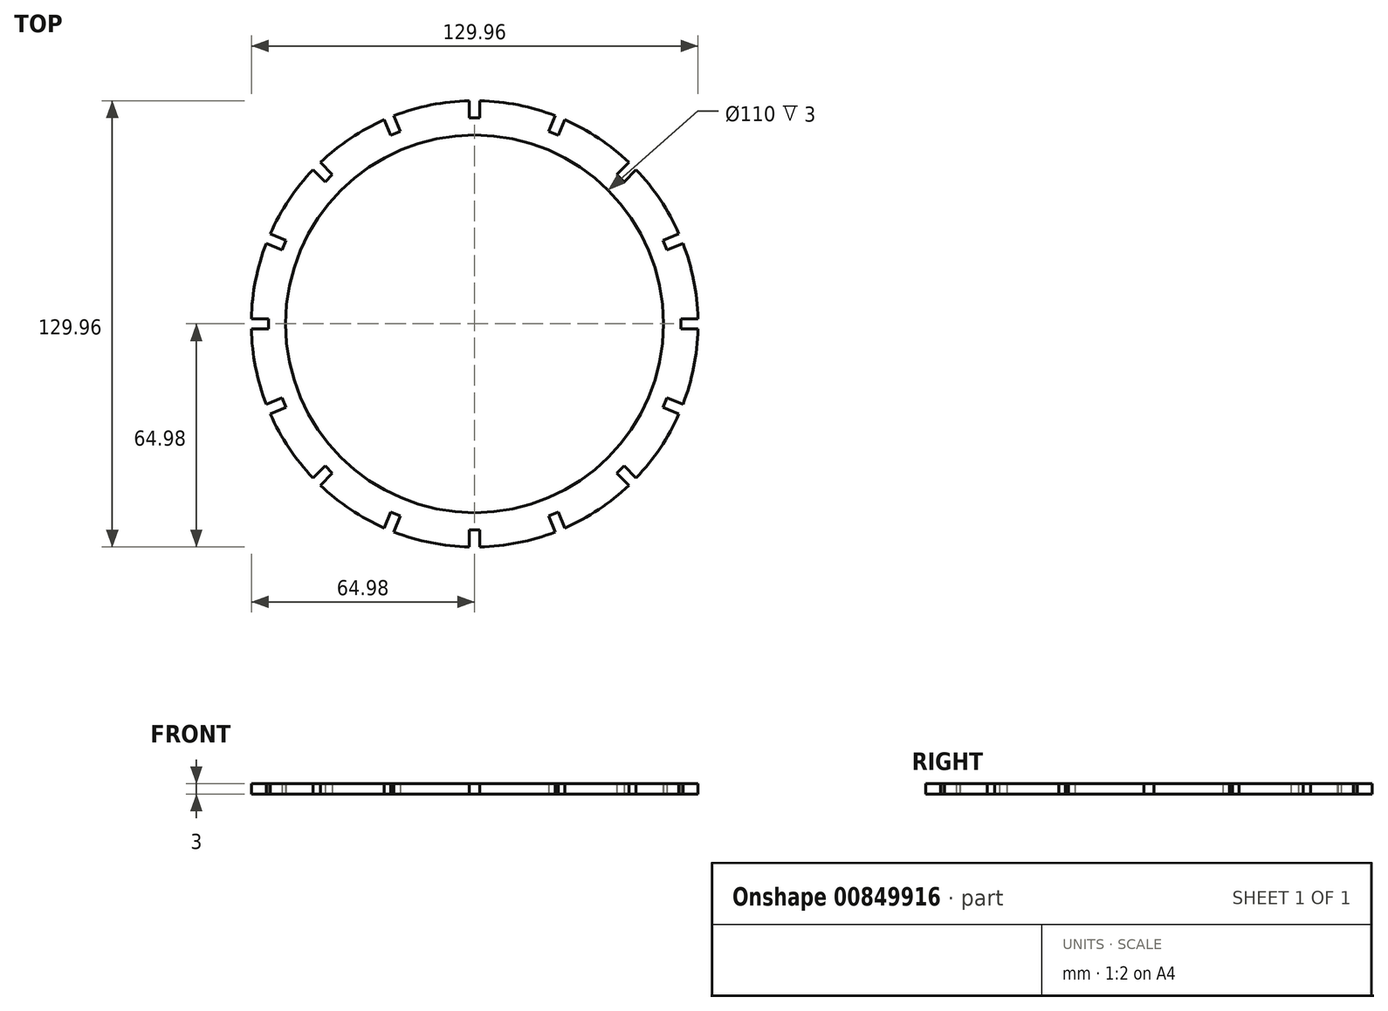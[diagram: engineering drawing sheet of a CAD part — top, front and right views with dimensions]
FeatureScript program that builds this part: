
annotation { "Feature Type Name" : "Feature", "Feature Type Description" : "" }
export const myFeature = defineFeature(function(context is Context, id is Id, definition is map)
    precondition{}
    {
        {
            var Q0;
            Q0=qCreatedBy(makeId("Top.planeOp"),FACE);
            var sketch = newSketch(context, id + "F0", { "sketchPlane" : qUnion([Q0])});
            skCircle(sketch, "E0", {"center": v(0, 0) * mm, "radius": 55 * mm});
            skCircle(sketch, "E1", {"center": v(0, 0) * mm, "radius": 65 * mm});
            skLineSegment(sketch, "E2", {"start": v(0, -60) * mm, "end": v(-1.5, -60) * mm});
            skLineSegment(sketch, "E3", {"start": v(-1.5, -60) * mm, "end": v(1.5, -60) * mm});
            skLineSegment(sketch, "E4", {"start": v(1.5, -60) * mm, "end": v(1.5, -64.98) * mm});
            skLineSegment(sketch, "E5", {"start": v(-1.5, -60) * mm, "end": v(-1.5, -64.98) * mm});
            skLineSegment(sketch, "E6.1.0", {"start": v(21.58, -56) * mm, "end": v(24.35, -54.86) * mm});
            skLineSegment(sketch, "E6.1.1", {"start": v(24.35, -54.86) * mm, "end": v(26.25, -59.46) * mm});
            skLineSegment(sketch, "E6.1.2", {"start": v(21.58, -56) * mm, "end": v(23.48, -60.61) * mm});
            skLineSegment(sketch, "E6.2.0", {"start": v(41.37, -43.49) * mm, "end": v(43.49, -41.37) * mm});
            skLineSegment(sketch, "E6.2.1", {"start": v(43.49, -41.37) * mm, "end": v(47.01, -44.89) * mm});
            skLineSegment(sketch, "E6.2.2", {"start": v(41.37, -43.49) * mm, "end": v(44.89, -47.01) * mm});
            skLineSegment(sketch, "E6.3.0", {"start": v(54.86, -24.35) * mm, "end": v(56, -21.58) * mm});
            skLineSegment(sketch, "E6.3.1", {"start": v(56, -21.58) * mm, "end": v(60.61, -23.48) * mm});
            skLineSegment(sketch, "E6.3.2", {"start": v(54.86, -24.35) * mm, "end": v(59.46, -26.25) * mm});
            skLineSegment(sketch, "E6.4.0", {"start": v(60, -1.5) * mm, "end": v(60, 1.5) * mm});
            skLineSegment(sketch, "E6.4.1", {"start": v(60, 1.5) * mm, "end": v(64.98, 1.5) * mm});
            skLineSegment(sketch, "E6.4.2", {"start": v(60, -1.5) * mm, "end": v(64.98, -1.5) * mm});
            skLineSegment(sketch, "E6.5.0", {"start": v(56, 21.58) * mm, "end": v(54.86, 24.35) * mm});
            skLineSegment(sketch, "E6.5.1", {"start": v(54.86, 24.35) * mm, "end": v(59.46, 26.25) * mm});
            skLineSegment(sketch, "E6.5.2", {"start": v(56, 21.58) * mm, "end": v(60.61, 23.48) * mm});
            skLineSegment(sketch, "E6.6.0", {"start": v(43.49, 41.37) * mm, "end": v(41.37, 43.49) * mm});
            skLineSegment(sketch, "E6.6.1", {"start": v(41.37, 43.49) * mm, "end": v(44.89, 47.01) * mm});
            skLineSegment(sketch, "E6.6.2", {"start": v(43.49, 41.37) * mm, "end": v(47.01, 44.89) * mm});
            skLineSegment(sketch, "E6.7.0", {"start": v(24.35, 54.86) * mm, "end": v(21.58, 56) * mm});
            skLineSegment(sketch, "E6.7.1", {"start": v(21.58, 56) * mm, "end": v(23.48, 60.61) * mm});
            skLineSegment(sketch, "E6.7.2", {"start": v(24.35, 54.86) * mm, "end": v(26.25, 59.46) * mm});
            skLineSegment(sketch, "E6.8.0", {"start": v(1.5, 60) * mm, "end": v(-1.5, 60) * mm});
            skLineSegment(sketch, "E6.8.1", {"start": v(-1.5, 60) * mm, "end": v(-1.5, 64.98) * mm});
            skLineSegment(sketch, "E6.8.2", {"start": v(1.5, 60) * mm, "end": v(1.5, 64.98) * mm});
            skLineSegment(sketch, "E6.9.0", {"start": v(-21.58, 56) * mm, "end": v(-24.35, 54.86) * mm});
            skLineSegment(sketch, "E6.9.1", {"start": v(-24.35, 54.86) * mm, "end": v(-26.25, 59.46) * mm});
            skLineSegment(sketch, "E6.9.2", {"start": v(-21.58, 56) * mm, "end": v(-23.48, 60.61) * mm});
            skLineSegment(sketch, "E6.10.0", {"start": v(-41.37, 43.49) * mm, "end": v(-43.49, 41.37) * mm});
            skLineSegment(sketch, "E6.10.1", {"start": v(-43.49, 41.37) * mm, "end": v(-47.01, 44.89) * mm});
            skLineSegment(sketch, "E6.10.2", {"start": v(-41.37, 43.49) * mm, "end": v(-44.89, 47.01) * mm});
            skLineSegment(sketch, "E6.11.0", {"start": v(-54.86, 24.35) * mm, "end": v(-56, 21.58) * mm});
            skLineSegment(sketch, "E6.11.1", {"start": v(-56, 21.58) * mm, "end": v(-60.61, 23.48) * mm});
            skLineSegment(sketch, "E6.11.2", {"start": v(-54.86, 24.35) * mm, "end": v(-59.46, 26.25) * mm});
            skLineSegment(sketch, "E6.12.0", {"start": v(-60, 1.5) * mm, "end": v(-60, -1.5) * mm});
            skLineSegment(sketch, "E6.12.1", {"start": v(-60, -1.5) * mm, "end": v(-64.98, -1.5) * mm});
            skLineSegment(sketch, "E6.12.2", {"start": v(-60, 1.5) * mm, "end": v(-64.98, 1.5) * mm});
            skLineSegment(sketch, "E6.13.0", {"start": v(-56, -21.58) * mm, "end": v(-54.86, -24.35) * mm});
            skLineSegment(sketch, "E6.13.1", {"start": v(-54.86, -24.35) * mm, "end": v(-59.46, -26.25) * mm});
            skLineSegment(sketch, "E6.13.2", {"start": v(-56, -21.58) * mm, "end": v(-60.61, -23.48) * mm});
            skLineSegment(sketch, "E6.14.0", {"start": v(-43.49, -41.37) * mm, "end": v(-41.37, -43.49) * mm});
            skLineSegment(sketch, "E6.14.1", {"start": v(-41.37, -43.49) * mm, "end": v(-44.89, -47.01) * mm});
            skLineSegment(sketch, "E6.14.2", {"start": v(-43.49, -41.37) * mm, "end": v(-47.01, -44.89) * mm});
            skLineSegment(sketch, "E6.15.0", {"start": v(-24.35, -54.86) * mm, "end": v(-21.58, -56) * mm});
            skLineSegment(sketch, "E6.15.1", {"start": v(-21.58, -56) * mm, "end": v(-23.48, -60.61) * mm});
            skLineSegment(sketch, "E6.15.2", {"start": v(-24.35, -54.86) * mm, "end": v(-26.25, -59.46) * mm});
            skSolve(sketch);
        }
        {
            var Q0;
            Q0=makeQuery(id+"F0.imprint","IMPRINT",FACE,{"disambiguationData":[TD([[makeQuery(id+"F0.imprint","IMPRINT",EDGE,{"derivedFrom":sQuery(id+"F0.wireOp",EDGE,"E0")}),-1.0]])]});
            extrude(context, id + "F1", {"entities" : qUnion([Q0]), "depth" : 3 * mm, "offsetDistance" : 25 * mm});
        }
    });
